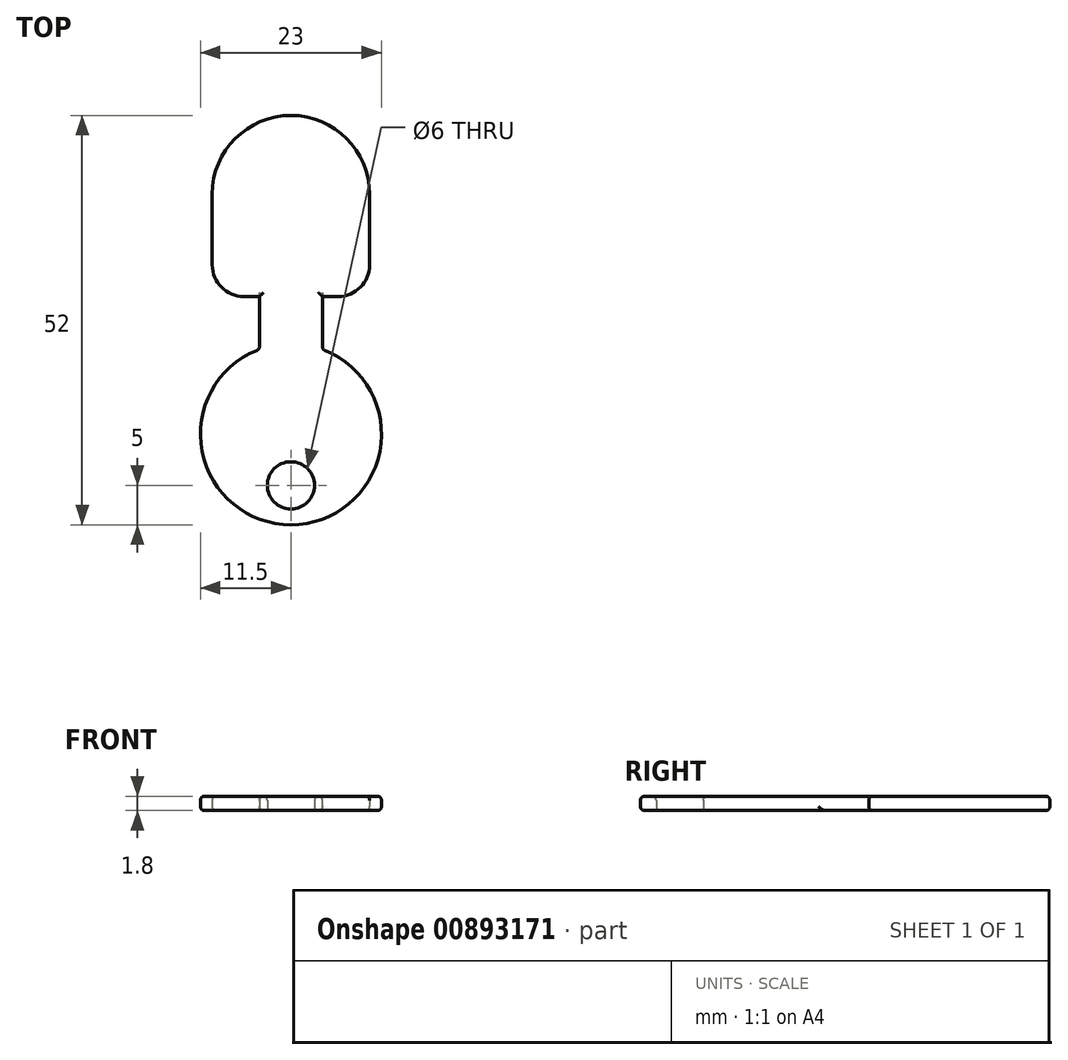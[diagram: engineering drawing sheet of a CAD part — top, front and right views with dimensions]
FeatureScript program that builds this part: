
annotation { "Feature Type Name" : "Feature", "Feature Type Description" : "" }
export const myFeature = defineFeature(function(context is Context, id is Id, definition is map)
    precondition{}
    {
        {
            var Q0;
            Q0=qCreatedBy(makeId("Top.planeOp"),FACE);
            var sketch = newSketch(context, id + "F0", { "sketchPlane" : qUnion([Q0])});
            skArc(sketch, "E0", {"start": v(-4, 10.78) * mm, "mid": v(0, -11.5) * mm, "end": v(4, 10.78) * mm});
            skLineSegment(sketch, "E1", {"start": v(4, 10.78) * mm, "end": v(4, 17.5) * mm});
            skLineSegment(sketch, "E2.MirrorCS", {"start": v(-4, 10.78) * mm, "end": v(-4, 17.5) * mm});
            skLineSegment(sketch, "E3", {"start": v(-10, 17.5) * mm, "end": v(-4, 17.5) * mm});
            skPoint(sketch, "E4.orphan", {"position": v(4, 36.17) * mm});
            skPoint(sketch, "E5.orphan", {"position": v(-4, 36.17) * mm});
            skLineSegment(sketch, "E6", {"start": v(10, 17.5) * mm, "end": v(10, 30.5) * mm});
            skLineSegment(sketch, "E7.MirrorCS", {"start": v(-10, 17.5) * mm, "end": v(-10, 30.5) * mm});
            skPoint(sketch, "E8.orphan", {"position": v(10, 55.2) * mm});
            skPoint(sketch, "E9.orphan", {"position": v(-10, 55.2) * mm});
            skArc(sketch, "E10", {"start": v(10, 30.5) * mm, "mid": v(0, 40.5) * mm, "end": v(-10, 30.5) * mm});
            skLineSegment(sketch, "E11.trimOffspring", {"start": v(4, 17.5) * mm, "end": v(10, 17.5) * mm});
            skCircle(sketch, "E12", {"center": v(0, -6.5) * mm, "radius": 3 * mm});
            skSolve(sketch);
        }
        {
            var Q0;
            Q0=makeQuery(id+"F0.imprint","IMPRINT",FACE,{"disambiguationData":[TD([[makeQuery(id+"F0.imprint","IMPRINT",EDGE,{"derivedFrom":sQuery(id+"F0.wireOp",EDGE,"E0")}),1.0]])]});
            extrude(context, id + "F1", {"entities" : qUnion([Q0]), "depth" : 1.8 * mm, "offsetDistance" : 25 * mm});
        }
        {
            var Q0;
            Q0=makeQuery(id+"F1.opExtrude","SWEPT_EDGE",EDGE,{"disambiguationData":[OSD([sQuery(id+"F0.wireOp",EDGE,"E6"),sQuery(id+"F0.wireOp",EDGE,"E11.trimOffspring")])]});
            fillet(context, id + "F2", {"entities" : qUnion([Q0]), "radius" : 4 * mm, "tangentPropagation" : true, "allowEdgeOverflow" : false});
        }
        {
            var Q0;
            Q0=makeQuery(id+"F1.opExtrude","SWEPT_EDGE",EDGE,{"disambiguationData":[OSD([sQuery(id+"F0.wireOp",EDGE,"E3"),sQuery(id+"F0.wireOp",EDGE,"E7.MirrorCS")])]});
            fillet(context, id + "F3", {"entities" : qUnion([Q0]), "radius" : 4 * mm, "tangentPropagation" : true, "allowEdgeOverflow" : false});
        }
        {
            var Q0;
            Q0=makeQuery(id+"F1.opExtrude","CAP_FACE",FACE,{"disambiguationData":[OSD([sQuery(id+"F0.wireOp",EDGE,"E0"),sQuery(id+"F0.wireOp",EDGE,"E1"),sQuery(id+"F0.wireOp",EDGE,"E2.MirrorCS"),sQuery(id+"F0.wireOp",EDGE,"E3"),sQuery(id+"F0.wireOp",EDGE,"E6"),sQuery(id+"F0.wireOp",EDGE,"E7.MirrorCS"),sQuery(id+"F0.wireOp",EDGE,"E10"),sQuery(id+"F0.wireOp",EDGE,"E11.trimOffspring"),sQuery(id+"F0.wireOp",EDGE,"E12")])],"isStart":false});
            var Q1;
            Q1=makeQuery(id+"F1.opExtrude","SWEPT_FACE",FACE,{"disambiguationData":[OSD([sQuery(id+"F0.wireOp",EDGE,"E0")])]});
            var Q2;
            Q2=makeQuery(id+"F1.opExtrude","CAP_EDGE",EDGE,{"disambiguationData":[OSD([sQuery(id+"F0.wireOp",EDGE,"E6")])],"isStart":true});
            var Q3;
            {var subQ0=sQuery(id+"F0.wireOp",EDGE,"E11.trimOffspring");var subQ1=sQuery(id+"F0.wireOp",EDGE,"E6");Q3=makeQuery(id+"F2.opFillet","BLEND_EDGE",EDGE,{"blendedFrom":[makeQuery(id+"F1.opExtrude","SWEPT_EDGE",EDGE,{"disambiguationData":[OSD([subQ1,subQ0])]}),makeQuery(id+"F1.opExtrude","CAP_FACE",FACE,{"disambiguationData":[OSD([sQuery(id+"F0.wireOp",EDGE,"E0"),sQuery(id+"F0.wireOp",EDGE,"E1"),sQuery(id+"F0.wireOp",EDGE,"E2.MirrorCS"),sQuery(id+"F0.wireOp",EDGE,"E3"),subQ1,sQuery(id+"F0.wireOp",EDGE,"E7.MirrorCS"),sQuery(id+"F0.wireOp",EDGE,"E10"),subQ0,sQuery(id+"F0.wireOp",EDGE,"E12")])],"isStart":true})],"blendedInto":[makeQuery(id+"F1.opExtrude","CAP_FACE",FACE,{"disambiguationData":[OSD([sQuery(id+"F0.wireOp",EDGE,"E0"),sQuery(id+"F0.wireOp",EDGE,"E1"),sQuery(id+"F0.wireOp",EDGE,"E2.MirrorCS"),sQuery(id+"F0.wireOp",EDGE,"E3"),subQ1,sQuery(id+"F0.wireOp",EDGE,"E7.MirrorCS"),sQuery(id+"F0.wireOp",EDGE,"E10"),subQ0,sQuery(id+"F0.wireOp",EDGE,"E12")])],"isStart":true})]});}
            var Q4;
            Q4=makeQuery(id+"F1.opExtrude","CAP_EDGE",EDGE,{"disambiguationData":[OSD([sQuery(id+"F0.wireOp",EDGE,"E11.trimOffspring")])],"isStart":true});
            fillet(context, id + "F4", {"entities" : qUnion([Q0, Q1, Q2, Q3, Q4]), "radius" : 0.5 * mm, "tangentPropagation" : true, "allowEdgeOverflow" : false});
        }
    });
